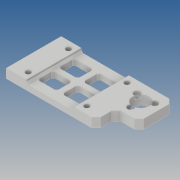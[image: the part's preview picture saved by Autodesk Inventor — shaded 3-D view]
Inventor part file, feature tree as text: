
AUTODESK INVENTOR PART (.ipt)
format: ipt  version: 2019 (Build 230136000, 136)  size: 279,040 bytes
history: native  units: mm
features: sketch x7, extrude x5, projected_geometry x5, chamfer x4, hole x2, pattern_circular x1
ambient origin geometry x8: Origin, YZ Plane, XZ Plane, XY Plane, X Axis, Y Axis, Z Axis, Center Point
bodies: Solide1 (feature_tree)
feature tree (24):
  extrude  "Extrusion1"  Depth=123.0mm
  extrude  "Extrusion2"  Depth=60.0mm
  hole  "Perçage1"  [1 undecoded]
  pattern_circular  "Réseau circulaire1"  [2 undecoded]
  hole  "Perçage2"  [1 undecoded]
  extrude  "Extrusion4"  Depth=18.0mm
  chamfer  "Chanfrein1"  Distance=10.0mm
  chamfer  "Chanfrein3"  Distance=11.0mm
  extrude  "Extrusion5"  Depth=30.0mm TaperAngle=360.0deg
  chamfer  "Chanfrein5"  Distance=22.0mm
  extrude  "Extrusion6"  Depth=11.0mm
  chamfer  "Chanfrein6"  Distance=9.0mm
  sketch  "Esquisse1"
  sketch  "Esquisse2"
  projected_geometry  "Boucle projetée1"
  sketch  "Esquisse4"
  projected_geometry  "Boucle projetée3"
  sketch  "Esquisse5"
  projected_geometry  "Boucle projetée4"
  sketch  "Esquisse6"
  projected_geometry  "Boucle projetée5"
  sketch  "Esquisse7"
  projected_geometry  "Boucle projetée6"
  sketch  "Esquisse8"
note: 4 required parameter values undecoded (feature->parameter linkage not recoverable at this tier; creation-order binding heuristic only, values carry confidence <= 0.55)
